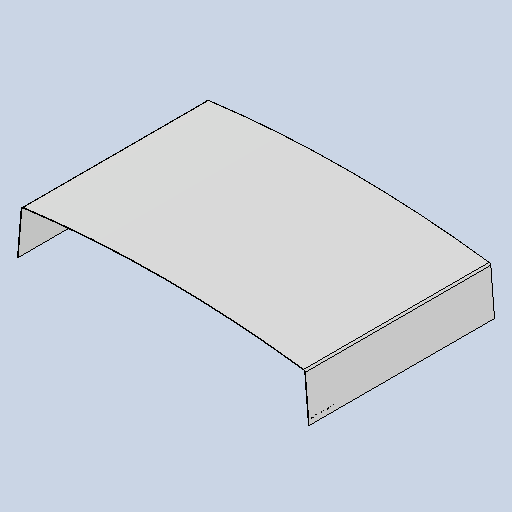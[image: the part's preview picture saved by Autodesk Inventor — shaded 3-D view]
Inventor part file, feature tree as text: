
AUTODESK INVENTOR PART (.ipt)
format: ipt  version: 2025 (Build 290162010, 162A)  size: 281,088 bytes
history: native  units: mm
features: other x7, sheet_metal_op x3, sketch x2, mirror x1
ambient origin geometry x8: Origin, YZ Plane, XZ Plane, XY Plane, X Axis, Y Axis, Z Axis, Center Point
bodies: Body1 (feature_tree)
feature tree (13):
  sheet_metal_op  "Contour Flange2"
  mirror  "Mirror2"
  other  "Mark1"
  other  "A-Side Definition"
  sketch  "Sketch1"  dims[d36=3.0mm]
  other  "Plate2"
  sheet_metal_op  "Bend2"
  sheet_metal_op  "Corner2"
  sketch  "Sketch2"  dims[d37=3.0mm d38=1.5mm d39=6.0mm d40=5.0mm d41=980.0mm d42=5.0mm d43=3.0mm d44=12.0mm d45=3.0mm d46=5.0mm d54=1500.0mm d55=2700.0mm d58=2100.0mm d65=8.0mm d66=8.0mm d78=3.0mm d80=3.0mm d83=8.0mm d113=50.0mm d114=50.0mm d115=3.0mm d121=10.0mm d122=241.9mm d124=16.546129mm d0=1980.030402mm d1=980.0mm]
  other  "Definition1"
  other  "Annotations"
  other  "Linear Dimension 1"
  other  "Linear Dimension 2"
